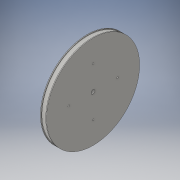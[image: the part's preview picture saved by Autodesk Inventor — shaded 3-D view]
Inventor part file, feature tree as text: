
AUTODESK INVENTOR PART (.ipt)
format: ipt  version: 2016 (Build 200138000, 138)  size: 162,816 bytes
history: native  units: in
note: dims shown in document units (in); Inventor stores cm internally (conversion verified against a paired STEP export)
features: sketch x6, extrude x4, hole x2
ambient origin geometry x8: Origin, YZ Plane, XZ Plane, XY Plane, X Axis, Y Axis, Z Axis, Center Point
bodies: Solid1 (feature_tree)
feature tree (12):
  extrude  "Extrusion1"  Depth=0.12in TaperAngle=0.0deg
  extrude  "Extrusion2"  Depth=0.02in TaperAngle=0.0deg
  extrude  "Extrusion3"  Depth=0.0394in
  hole  "Hole1"  [1 undecoded]
  hole  "Hole2"  [1 undecoded]
  extrude  "Extrusion4"  [1 undecoded]
  sketch  "Sketch1"  dims[d0=2.4in d1=0.12in d2=0.0in]
  sketch  "Sketch2"  dims[d3=0.02in d4=0.0in d5=0.02in d6=0.0in]
  sketch  "Sketch3"  dims[d7=0.1024in]
  sketch  "Sketch4"  dims[d8=0.1024in d9=0.75in d10=0.375in d11=0.25in d12=0.5635in d13=1.0in d14=0.8108in d19=0.0394in]
  sketch  "Sketch5"  dims[d20=0.0394in d21=0.0394in]
  sketch  "Sketch6"  dims[d22=0.0394in d23=0.0394in d24=0.75in d25=0.375in d26=0.25in d27=0.5635in d28=1.0in d29=0.8108in d30=0.086in d31=0.0in]
note: 3 required parameter values undecoded (feature->parameter linkage not recoverable at this tier; creation-order binding heuristic only, values carry confidence <= 0.55)
